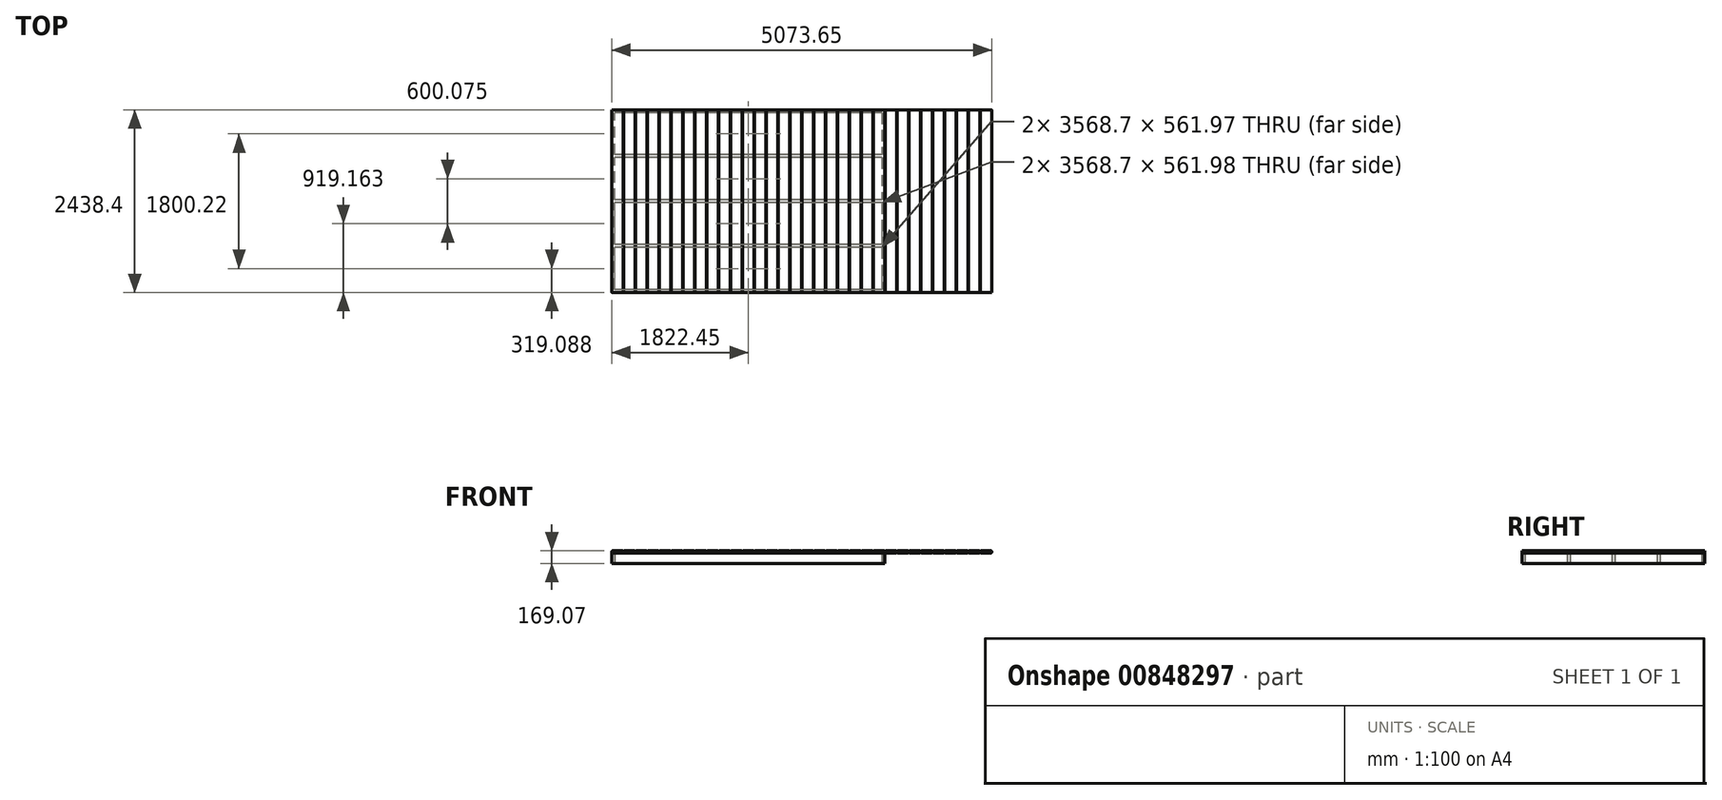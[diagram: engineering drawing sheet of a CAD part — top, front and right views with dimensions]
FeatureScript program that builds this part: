
annotation { "Feature Type Name" : "Feature", "Feature Type Description" : "" }
export const myFeature = defineFeature(function(context is Context, id is Id, definition is map)
    precondition{}
    {
        {
            var Q0;
            Q0=qCreatedBy(makeId("Top.planeOp"),FACE);
            var sketch = newSketch(context, id + "F0", { "sketchPlane" : qUnion([Q0])});
            skLineSegment(sketch, "E0.bottom", {"start": v(1784.35, 1181.1) * mm, "end": v(-1784.35, 1181.1) * mm});
            skLineSegment(sketch, "E0.top", {"start": v(1784.35, 1219.2) * mm, "end": v(-1784.35, 1219.2) * mm});
            skLineSegment(sketch, "E0.left", {"start": v(1784.35, 1181.1) * mm, "end": v(1784.35, 1219.2) * mm});
            skLineSegment(sketch, "E0.right", {"start": v(-1784.35, 1181.1) * mm, "end": v(-1784.35, 1219.2) * mm});
            skLineSegment(sketch, "E1.0.1.0", {"start": v(1784.35, 581.02) * mm, "end": v(-1784.35, 581.02) * mm});
            skLineSegment(sketch, "E1.0.1.1", {"start": v(1784.35, 619.12) * mm, "end": v(-1784.35, 619.12) * mm});
            skLineSegment(sketch, "E1.0.1.2", {"start": v(1784.35, 581.03) * mm, "end": v(1784.35, 619.12) * mm});
            skLineSegment(sketch, "E1.0.1.3", {"start": v(-1784.35, 581.02) * mm, "end": v(-1784.35, 619.12) * mm});
            skLineSegment(sketch, "E1.0.2.0", {"start": v(1784.35, -19.05) * mm, "end": v(-1784.35, -19.05) * mm});
            skLineSegment(sketch, "E1.0.2.1", {"start": v(1784.35, 19.05) * mm, "end": v(-1784.35, 19.05) * mm});
            skLineSegment(sketch, "E1.0.2.2", {"start": v(1784.35, -19.05) * mm, "end": v(1784.35, 19.05) * mm});
            skLineSegment(sketch, "E1.0.2.3", {"start": v(-1784.35, -19.05) * mm, "end": v(-1784.35, 19.05) * mm});
            skLineSegment(sketch, "E1.0.3.0", {"start": v(1784.35, -619.13) * mm, "end": v(-1784.35, -619.13) * mm});
            skLineSegment(sketch, "E1.0.3.1", {"start": v(1784.35, -581.03) * mm, "end": v(-1784.35, -581.03) * mm});
            skLineSegment(sketch, "E1.0.3.2", {"start": v(1784.35, -619.12) * mm, "end": v(1784.35, -581.03) * mm});
            skLineSegment(sketch, "E1.0.3.3", {"start": v(-1784.35, -619.13) * mm, "end": v(-1784.35, -581.03) * mm});
            skLineSegment(sketch, "E1.direction1", {"start": v(-1784.35, 1181.1) * mm, "end": v(110.9, 1181.1) * mm, "construction": true});
            skLineSegment(sketch, "E1.direction2", {"start": v(-1784.35, 1181.1) * mm, "end": v(-1784.35, 581.02) * mm, "construction": true});
            skLineSegment(sketch, "E2.0.0.4", {"start": v(1784.35, -1219.2) * mm, "end": v(-1784.35, -1219.2) * mm});
            skLineSegment(sketch, "E2.3.0.4", {"start": v(1784.35, -1181.1) * mm, "end": v(-1784.35, -1181.1) * mm});
            skLineSegment(sketch, "E2.6.0.4", {"start": v(1784.35, -1219.2) * mm, "end": v(1784.35, -1181.1) * mm});
            skLineSegment(sketch, "E2.9.0.4", {"start": v(-1784.35, -1219.2) * mm, "end": v(-1784.35, -1181.1) * mm});
            skLineSegment(sketch, "E3.bottom", {"start": v(-1784.35, -1219.2) * mm, "end": v(-1822.45, -1219.2) * mm});
            skLineSegment(sketch, "E3.top", {"start": v(-1784.35, 1219.2) * mm, "end": v(-1822.45, 1219.2) * mm});
            skLineSegment(sketch, "E3.left", {"start": v(-1784.35, -1219.2) * mm, "end": v(-1784.35, 1219.2) * mm});
            skLineSegment(sketch, "E3.right", {"start": v(-1822.45, -1219.2) * mm, "end": v(-1822.45, 1219.2) * mm});
            skLineSegment(sketch, "E4.bottom", {"start": v(1784.35, 1219.2) * mm, "end": v(1822.45, 1219.2) * mm});
            skLineSegment(sketch, "E4.top", {"start": v(1784.35, -1219.2) * mm, "end": v(1822.45, -1219.2) * mm});
            skLineSegment(sketch, "E4.left", {"start": v(1784.35, 1219.2) * mm, "end": v(1784.35, -1219.2) * mm});
            skLineSegment(sketch, "E4.right", {"start": v(1822.45, 1219.2) * mm, "end": v(1822.45, -1219.2) * mm});
            skLineSegment(sketch, "E5", {"start": v(1784.35, -1219.2) * mm, "end": v(-1784.35, 1219.2) * mm, "construction": true});
            skSolve(sketch);
        }
        {
            var Q0;
            {var subQ0=sQuery(id+"F0.wireOp",EDGE,"E0.bottom");Q0=makeQuery(id+"F0.imprint","IMPRINT",FACE,{"disambiguationData":[TD([[makeQuery(id+"F0.imprint","IMPRINT",EDGE,{"derivedFrom":subQ0}),-1.0]])]});}
            var Q1;
            {var subQ8=sQuery(id+"F0.wireOp",EDGE,"E3.bottom");Q1=makeQuery(id+"F0.imprint","IMPRINT",FACE,{"disambiguationData":[TD([[makeQuery(id+"F0.imprint","IMPRINT",EDGE,{"derivedFrom":subQ8}),-1.0]])]});}
            var Q2;
            {var subQ0=sQuery(id+"F0.wireOp",EDGE,"E1.0.1.0");Q2=makeQuery(id+"F0.imprint","IMPRINT",FACE,{"disambiguationData":[TD([[makeQuery(id+"F0.imprint","IMPRINT",EDGE,{"derivedFrom":subQ0}),-1.0]])]});}
            var Q3;
            {var subQ0=sQuery(id+"F0.wireOp",EDGE,"E1.0.2.0");Q3=makeQuery(id+"F0.imprint","IMPRINT",FACE,{"disambiguationData":[TD([[makeQuery(id+"F0.imprint","IMPRINT",EDGE,{"derivedFrom":subQ0}),-1.0]])]});}
            var Q4;
            {var subQ0=sQuery(id+"F0.wireOp",EDGE,"E1.0.3.0");Q4=makeQuery(id+"F0.imprint","IMPRINT",FACE,{"disambiguationData":[TD([[makeQuery(id+"F0.imprint","IMPRINT",EDGE,{"derivedFrom":subQ0}),-1.0]])]});}
            var Q5;
            {var subQ0=sQuery(id+"F0.wireOp",EDGE,"E2.0.0.4");Q5=makeQuery(id+"F0.imprint","IMPRINT",FACE,{"disambiguationData":[TD([[makeQuery(id+"F0.imprint","IMPRINT",EDGE,{"derivedFrom":subQ0}),-1.0]])]});}
            var Q6;
            {var subQ8=sQuery(id+"F0.wireOp",EDGE,"E4.bottom");Q6=makeQuery(id+"F0.imprint","IMPRINT",FACE,{"disambiguationData":[TD([[makeQuery(id+"F0.imprint","IMPRINT",EDGE,{"derivedFrom":subQ8}),-1.0]])]});}
            extrude(context, id + "F1", {"entities" : qUnion([Q0, Q1, Q2, Q3, Q4, Q5, Q6]), "depth" : 139.7 * mm, "offsetDistance" : 25.4 * mm});
        }
        {
            var Q0;
            Q0=makeQuery(id+"F1.opExtrude","SWEPT_FACE",FACE,{"disambiguationData":[OSD([sQuery(id+"F0.wireOp",EDGE,"E2.0.0.4"),sQuery(id+"F0.wireOp",EDGE,"E3.bottom"),sQuery(id+"F0.wireOp",EDGE,"E4.top")])]});
            var sketch = newSketch(context, id + "F2", { "sketchPlane" : qUnion([Q0])});
            skLineSegment(sketch, "E6.bottom", {"start": v(-1809.75, 139.7) * mm, "end": v(-1682.75, 139.7) * mm});
            skLineSegment(sketch, "E6.top", {"start": v(-1809.75, 169.07) * mm, "end": v(-1682.75, 169.07) * mm});
            skLineSegment(sketch, "E6.left", {"start": v(-1822.45, 152.4) * mm, "end": v(-1822.45, 156.37) * mm});
            skLineSegment(sketch, "E6.right", {"start": v(-1670.05, 152.4) * mm, "end": v(-1670.05, 156.37) * mm});
            skPoint(sketch, "E7.visualSharp", {"position": v(-1822.45, 169.07) * mm});
            skArc(sketch, "E7.filletArc", {"start": v(-1809.75, 169.07) * mm, "mid": v(-1818.73, 165.35) * mm, "end": v(-1822.45, 156.37) * mm});
            skPoint(sketch, "E8.visualSharp", {"position": v(-1670.05, 169.07) * mm});
            skArc(sketch, "E8.filletArc", {"start": v(-1670.05, 156.37) * mm, "mid": v(-1673.77, 165.35) * mm, "end": v(-1682.75, 169.07) * mm});
            skPoint(sketch, "E9.visualSharp", {"position": v(-1670.05, 139.7) * mm});
            skArc(sketch, "E9.filletArc", {"start": v(-1682.75, 139.7) * mm, "mid": v(-1673.77, 143.42) * mm, "end": v(-1670.05, 152.4) * mm});
            skPoint(sketch, "E10.visualSharp", {"position": v(-1822.45, 139.7) * mm});
            skArc(sketch, "E10.filletArc", {"start": v(-1822.45, 152.4) * mm, "mid": v(-1818.73, 143.42) * mm, "end": v(-1809.75, 139.7) * mm});
            skPoint(sketch, "E11.1.0.0", {"position": v(-1663.7, 139.7) * mm});
            skPoint(sketch, "E11.1.0.1", {"position": v(-1511.3, 139.7) * mm});
            skPoint(sketch, "E11.1.0.2", {"position": v(-1663.7, 169.07) * mm});
            skLineSegment(sketch, "E11.1.0.3", {"start": v(-1651, 169.07) * mm, "end": v(-1524, 169.07) * mm});
            skLineSegment(sketch, "E11.1.0.4", {"start": v(-1651, 139.7) * mm, "end": v(-1524, 139.7) * mm});
            skPoint(sketch, "E11.1.0.5", {"position": v(-1511.3, 169.07) * mm});
            skArc(sketch, "E11.1.0.6", {"start": v(-1663.7, 152.4) * mm, "mid": v(-1659.98, 143.42) * mm, "end": v(-1651, 139.7) * mm});
            skArc(sketch, "E11.1.0.7", {"start": v(-1524, 139.7) * mm, "mid": v(-1515.02, 143.42) * mm, "end": v(-1511.3, 152.4) * mm});
            skArc(sketch, "E11.1.0.8", {"start": v(-1651, 169.07) * mm, "mid": v(-1659.98, 165.35) * mm, "end": v(-1663.7, 156.37) * mm});
            skArc(sketch, "E11.1.0.9", {"start": v(-1511.3, 156.37) * mm, "mid": v(-1515.02, 165.35) * mm, "end": v(-1524, 169.07) * mm});
            skLineSegment(sketch, "E11.1.0.10", {"start": v(-1511.3, 152.4) * mm, "end": v(-1511.3, 156.37) * mm});
            skLineSegment(sketch, "E11.1.0.11", {"start": v(-1663.7, 152.4) * mm, "end": v(-1663.7, 156.37) * mm});
            skPoint(sketch, "E11.2.0.0", {"position": v(-1504.95, 139.7) * mm});
            skPoint(sketch, "E11.2.0.1", {"position": v(-1352.55, 139.7) * mm});
            skPoint(sketch, "E11.2.0.2", {"position": v(-1504.95, 169.07) * mm});
            skLineSegment(sketch, "E11.2.0.3", {"start": v(-1492.25, 169.07) * mm, "end": v(-1365.25, 169.07) * mm});
            skLineSegment(sketch, "E11.2.0.4", {"start": v(-1492.25, 139.7) * mm, "end": v(-1365.25, 139.7) * mm});
            skPoint(sketch, "E11.2.0.5", {"position": v(-1352.55, 169.07) * mm});
            skArc(sketch, "E11.2.0.6", {"start": v(-1504.95, 152.4) * mm, "mid": v(-1501.23, 143.42) * mm, "end": v(-1492.25, 139.7) * mm});
            skArc(sketch, "E11.2.0.7", {"start": v(-1365.25, 139.7) * mm, "mid": v(-1356.27, 143.42) * mm, "end": v(-1352.55, 152.4) * mm});
            skArc(sketch, "E11.2.0.8", {"start": v(-1492.25, 169.07) * mm, "mid": v(-1501.23, 165.35) * mm, "end": v(-1504.95, 156.37) * mm});
            skArc(sketch, "E11.2.0.9", {"start": v(-1352.55, 156.37) * mm, "mid": v(-1356.27, 165.35) * mm, "end": v(-1365.25, 169.07) * mm});
            skLineSegment(sketch, "E11.2.0.10", {"start": v(-1352.55, 152.4) * mm, "end": v(-1352.55, 156.37) * mm});
            skLineSegment(sketch, "E11.2.0.11", {"start": v(-1504.95, 152.4) * mm, "end": v(-1504.95, 156.37) * mm});
            skPoint(sketch, "E11.3.0.0", {"position": v(-1346.2, 139.7) * mm});
            skPoint(sketch, "E11.3.0.1", {"position": v(-1193.8, 139.7) * mm});
            skPoint(sketch, "E11.3.0.2", {"position": v(-1346.2, 169.07) * mm});
            skLineSegment(sketch, "E11.3.0.3", {"start": v(-1333.5, 169.07) * mm, "end": v(-1206.5, 169.07) * mm});
            skLineSegment(sketch, "E11.3.0.4", {"start": v(-1333.5, 139.7) * mm, "end": v(-1206.5, 139.7) * mm});
            skPoint(sketch, "E11.3.0.5", {"position": v(-1193.8, 169.07) * mm});
            skArc(sketch, "E11.3.0.6", {"start": v(-1346.2, 152.4) * mm, "mid": v(-1342.48, 143.42) * mm, "end": v(-1333.5, 139.7) * mm});
            skArc(sketch, "E11.3.0.7", {"start": v(-1206.5, 139.7) * mm, "mid": v(-1197.52, 143.42) * mm, "end": v(-1193.8, 152.4) * mm});
            skArc(sketch, "E11.3.0.8", {"start": v(-1333.5, 169.07) * mm, "mid": v(-1342.48, 165.35) * mm, "end": v(-1346.2, 156.37) * mm});
            skArc(sketch, "E11.3.0.9", {"start": v(-1193.8, 156.37) * mm, "mid": v(-1197.52, 165.35) * mm, "end": v(-1206.5, 169.07) * mm});
            skLineSegment(sketch, "E11.3.0.10", {"start": v(-1193.8, 152.4) * mm, "end": v(-1193.8, 156.37) * mm});
            skLineSegment(sketch, "E11.3.0.11", {"start": v(-1346.2, 152.4) * mm, "end": v(-1346.2, 156.37) * mm});
            skPoint(sketch, "E11.4.0.0", {"position": v(-1187.45, 139.7) * mm});
            skPoint(sketch, "E11.4.0.1", {"position": v(-1035.05, 139.7) * mm});
            skPoint(sketch, "E11.4.0.2", {"position": v(-1187.45, 169.07) * mm});
            skLineSegment(sketch, "E11.4.0.3", {"start": v(-1174.75, 169.07) * mm, "end": v(-1047.75, 169.07) * mm});
            skLineSegment(sketch, "E11.4.0.4", {"start": v(-1174.75, 139.7) * mm, "end": v(-1047.75, 139.7) * mm});
            skPoint(sketch, "E11.4.0.5", {"position": v(-1035.05, 169.07) * mm});
            skArc(sketch, "E11.4.0.6", {"start": v(-1187.45, 152.4) * mm, "mid": v(-1183.73, 143.42) * mm, "end": v(-1174.75, 139.7) * mm});
            skArc(sketch, "E11.4.0.7", {"start": v(-1047.75, 139.7) * mm, "mid": v(-1038.77, 143.42) * mm, "end": v(-1035.05, 152.4) * mm});
            skArc(sketch, "E11.4.0.8", {"start": v(-1174.75, 169.07) * mm, "mid": v(-1183.73, 165.35) * mm, "end": v(-1187.45, 156.37) * mm});
            skArc(sketch, "E11.4.0.9", {"start": v(-1035.05, 156.37) * mm, "mid": v(-1038.77, 165.35) * mm, "end": v(-1047.75, 169.07) * mm});
            skLineSegment(sketch, "E11.4.0.10", {"start": v(-1035.05, 152.4) * mm, "end": v(-1035.05, 156.37) * mm});
            skLineSegment(sketch, "E11.4.0.11", {"start": v(-1187.45, 152.4) * mm, "end": v(-1187.45, 156.37) * mm});
            skPoint(sketch, "E11.5.0.0", {"position": v(-1028.7, 139.7) * mm});
            skPoint(sketch, "E11.5.0.1", {"position": v(-876.3, 139.7) * mm});
            skPoint(sketch, "E11.5.0.2", {"position": v(-1028.7, 169.07) * mm});
            skLineSegment(sketch, "E11.5.0.3", {"start": v(-1016, 169.07) * mm, "end": v(-889, 169.07) * mm});
            skLineSegment(sketch, "E11.5.0.4", {"start": v(-1016, 139.7) * mm, "end": v(-889, 139.7) * mm});
            skPoint(sketch, "E11.5.0.5", {"position": v(-876.3, 169.07) * mm});
            skArc(sketch, "E11.5.0.6", {"start": v(-1028.7, 152.4) * mm, "mid": v(-1024.98, 143.42) * mm, "end": v(-1016, 139.7) * mm});
            skArc(sketch, "E11.5.0.7", {"start": v(-889, 139.7) * mm, "mid": v(-880.02, 143.42) * mm, "end": v(-876.3, 152.4) * mm});
            skArc(sketch, "E11.5.0.8", {"start": v(-1016, 169.07) * mm, "mid": v(-1024.98, 165.35) * mm, "end": v(-1028.7, 156.37) * mm});
            skArc(sketch, "E11.5.0.9", {"start": v(-876.3, 156.37) * mm, "mid": v(-880.02, 165.35) * mm, "end": v(-889, 169.07) * mm});
            skLineSegment(sketch, "E11.5.0.10", {"start": v(-876.3, 152.4) * mm, "end": v(-876.3, 156.37) * mm});
            skLineSegment(sketch, "E11.5.0.11", {"start": v(-1028.7, 152.4) * mm, "end": v(-1028.7, 156.37) * mm});
            skPoint(sketch, "E11.6.0.0", {"position": v(-869.95, 139.7) * mm});
            skPoint(sketch, "E11.6.0.1", {"position": v(-717.55, 139.7) * mm});
            skPoint(sketch, "E11.6.0.2", {"position": v(-869.95, 169.07) * mm});
            skLineSegment(sketch, "E11.6.0.3", {"start": v(-857.25, 169.07) * mm, "end": v(-730.25, 169.07) * mm});
            skLineSegment(sketch, "E11.6.0.4", {"start": v(-857.25, 139.7) * mm, "end": v(-730.25, 139.7) * mm});
            skPoint(sketch, "E11.6.0.5", {"position": v(-717.55, 169.07) * mm});
            skArc(sketch, "E11.6.0.6", {"start": v(-869.95, 152.4) * mm, "mid": v(-866.23, 143.42) * mm, "end": v(-857.25, 139.7) * mm});
            skArc(sketch, "E11.6.0.7", {"start": v(-730.25, 139.7) * mm, "mid": v(-721.27, 143.42) * mm, "end": v(-717.55, 152.4) * mm});
            skArc(sketch, "E11.6.0.8", {"start": v(-857.25, 169.07) * mm, "mid": v(-866.23, 165.35) * mm, "end": v(-869.95, 156.37) * mm});
            skArc(sketch, "E11.6.0.9", {"start": v(-717.55, 156.37) * mm, "mid": v(-721.27, 165.35) * mm, "end": v(-730.25, 169.07) * mm});
            skLineSegment(sketch, "E11.6.0.10", {"start": v(-717.55, 152.4) * mm, "end": v(-717.55, 156.37) * mm});
            skLineSegment(sketch, "E11.6.0.11", {"start": v(-869.95, 152.4) * mm, "end": v(-869.95, 156.37) * mm});
            skPoint(sketch, "E11.7.0.0", {"position": v(-711.2, 139.7) * mm});
            skPoint(sketch, "E11.7.0.1", {"position": v(-558.8, 139.7) * mm});
            skPoint(sketch, "E11.7.0.2", {"position": v(-711.2, 169.07) * mm});
            skLineSegment(sketch, "E11.7.0.3", {"start": v(-698.5, 169.07) * mm, "end": v(-571.5, 169.07) * mm});
            skLineSegment(sketch, "E11.7.0.4", {"start": v(-698.5, 139.7) * mm, "end": v(-571.5, 139.7) * mm});
            skPoint(sketch, "E11.7.0.5", {"position": v(-558.8, 169.07) * mm});
            skArc(sketch, "E11.7.0.6", {"start": v(-711.2, 152.4) * mm, "mid": v(-707.48, 143.42) * mm, "end": v(-698.5, 139.7) * mm});
            skArc(sketch, "E11.7.0.7", {"start": v(-571.5, 139.7) * mm, "mid": v(-562.52, 143.42) * mm, "end": v(-558.8, 152.4) * mm});
            skArc(sketch, "E11.7.0.8", {"start": v(-698.5, 169.07) * mm, "mid": v(-707.48, 165.35) * mm, "end": v(-711.2, 156.37) * mm});
            skArc(sketch, "E11.7.0.9", {"start": v(-558.8, 156.37) * mm, "mid": v(-562.52, 165.35) * mm, "end": v(-571.5, 169.07) * mm});
            skLineSegment(sketch, "E11.7.0.10", {"start": v(-558.8, 152.4) * mm, "end": v(-558.8, 156.37) * mm});
            skLineSegment(sketch, "E11.7.0.11", {"start": v(-711.2, 152.4) * mm, "end": v(-711.2, 156.37) * mm});
            skPoint(sketch, "E11.8.0.0", {"position": v(-552.45, 139.7) * mm});
            skPoint(sketch, "E11.8.0.1", {"position": v(-400.05, 139.7) * mm});
            skPoint(sketch, "E11.8.0.2", {"position": v(-552.45, 169.07) * mm});
            skLineSegment(sketch, "E11.8.0.3", {"start": v(-539.75, 169.07) * mm, "end": v(-412.75, 169.07) * mm});
            skLineSegment(sketch, "E11.8.0.4", {"start": v(-539.75, 139.7) * mm, "end": v(-412.75, 139.7) * mm});
            skPoint(sketch, "E11.8.0.5", {"position": v(-400.05, 169.07) * mm});
            skArc(sketch, "E11.8.0.6", {"start": v(-552.45, 152.4) * mm, "mid": v(-548.73, 143.42) * mm, "end": v(-539.75, 139.7) * mm});
            skArc(sketch, "E11.8.0.7", {"start": v(-412.75, 139.7) * mm, "mid": v(-403.77, 143.42) * mm, "end": v(-400.05, 152.4) * mm});
            skArc(sketch, "E11.8.0.8", {"start": v(-539.75, 169.07) * mm, "mid": v(-548.73, 165.35) * mm, "end": v(-552.45, 156.37) * mm});
            skArc(sketch, "E11.8.0.9", {"start": v(-400.05, 156.37) * mm, "mid": v(-403.77, 165.35) * mm, "end": v(-412.75, 169.07) * mm});
            skLineSegment(sketch, "E11.8.0.10", {"start": v(-400.05, 152.4) * mm, "end": v(-400.05, 156.37) * mm});
            skLineSegment(sketch, "E11.8.0.11", {"start": v(-552.45, 152.4) * mm, "end": v(-552.45, 156.37) * mm});
            skPoint(sketch, "E11.9.0.0", {"position": v(-393.7, 139.7) * mm});
            skPoint(sketch, "E11.9.0.1", {"position": v(-241.3, 139.7) * mm});
            skPoint(sketch, "E11.9.0.2", {"position": v(-393.7, 169.07) * mm});
            skLineSegment(sketch, "E11.9.0.3", {"start": v(-381, 169.07) * mm, "end": v(-254, 169.07) * mm});
            skLineSegment(sketch, "E11.9.0.4", {"start": v(-381, 139.7) * mm, "end": v(-254, 139.7) * mm});
            skPoint(sketch, "E11.9.0.5", {"position": v(-241.3, 169.07) * mm});
            skArc(sketch, "E11.9.0.6", {"start": v(-393.7, 152.4) * mm, "mid": v(-389.98, 143.42) * mm, "end": v(-381, 139.7) * mm});
            skArc(sketch, "E11.9.0.7", {"start": v(-254, 139.7) * mm, "mid": v(-245.02, 143.42) * mm, "end": v(-241.3, 152.4) * mm});
            skArc(sketch, "E11.9.0.8", {"start": v(-381, 169.07) * mm, "mid": v(-389.98, 165.35) * mm, "end": v(-393.7, 156.37) * mm});
            skArc(sketch, "E11.9.0.9", {"start": v(-241.3, 156.37) * mm, "mid": v(-245.02, 165.35) * mm, "end": v(-254, 169.07) * mm});
            skLineSegment(sketch, "E11.9.0.10", {"start": v(-241.3, 152.4) * mm, "end": v(-241.3, 156.37) * mm});
            skLineSegment(sketch, "E11.9.0.11", {"start": v(-393.7, 152.4) * mm, "end": v(-393.7, 156.37) * mm});
            skPoint(sketch, "E11.10.0.0", {"position": v(-234.95, 139.7) * mm});
            skPoint(sketch, "E11.10.0.1", {"position": v(-82.55, 139.7) * mm});
            skPoint(sketch, "E11.10.0.2", {"position": v(-234.95, 169.07) * mm});
            skLineSegment(sketch, "E11.10.0.3", {"start": v(-222.25, 169.07) * mm, "end": v(-95.25, 169.07) * mm});
            skLineSegment(sketch, "E11.10.0.4", {"start": v(-222.25, 139.7) * mm, "end": v(-95.25, 139.7) * mm});
            skPoint(sketch, "E11.10.0.5", {"position": v(-82.55, 169.07) * mm});
            skArc(sketch, "E11.10.0.6", {"start": v(-234.95, 152.4) * mm, "mid": v(-231.23, 143.42) * mm, "end": v(-222.25, 139.7) * mm});
            skArc(sketch, "E11.10.0.7", {"start": v(-95.25, 139.7) * mm, "mid": v(-86.27, 143.42) * mm, "end": v(-82.55, 152.4) * mm});
            skArc(sketch, "E11.10.0.8", {"start": v(-222.25, 169.07) * mm, "mid": v(-231.23, 165.35) * mm, "end": v(-234.95, 156.37) * mm});
            skArc(sketch, "E11.10.0.9", {"start": v(-82.55, 156.37) * mm, "mid": v(-86.27, 165.35) * mm, "end": v(-95.25, 169.07) * mm});
            skLineSegment(sketch, "E11.10.0.10", {"start": v(-82.55, 152.4) * mm, "end": v(-82.55, 156.37) * mm});
            skLineSegment(sketch, "E11.10.0.11", {"start": v(-234.95, 152.4) * mm, "end": v(-234.95, 156.37) * mm});
            skPoint(sketch, "E11.11.0.0", {"position": v(-76.2, 139.7) * mm});
            skPoint(sketch, "E11.11.0.1", {"position": v(76.2, 139.7) * mm});
            skPoint(sketch, "E11.11.0.2", {"position": v(-76.2, 169.07) * mm});
            skLineSegment(sketch, "E11.11.0.3", {"start": v(-63.5, 169.07) * mm, "end": v(63.5, 169.07) * mm});
            skLineSegment(sketch, "E11.11.0.4", {"start": v(-63.5, 139.7) * mm, "end": v(63.5, 139.7) * mm});
            skPoint(sketch, "E11.11.0.5", {"position": v(76.2, 169.07) * mm});
            skArc(sketch, "E11.11.0.6", {"start": v(-76.2, 152.4) * mm, "mid": v(-72.48, 143.42) * mm, "end": v(-63.5, 139.7) * mm});
            skArc(sketch, "E11.11.0.7", {"start": v(63.5, 139.7) * mm, "mid": v(72.48, 143.42) * mm, "end": v(76.2, 152.4) * mm});
            skArc(sketch, "E11.11.0.8", {"start": v(-63.5, 169.07) * mm, "mid": v(-72.48, 165.35) * mm, "end": v(-76.2, 156.37) * mm});
            skArc(sketch, "E11.11.0.9", {"start": v(76.2, 156.37) * mm, "mid": v(72.48, 165.35) * mm, "end": v(63.5, 169.07) * mm});
            skLineSegment(sketch, "E11.11.0.10", {"start": v(76.2, 152.4) * mm, "end": v(76.2, 156.37) * mm});
            skLineSegment(sketch, "E11.11.0.11", {"start": v(-76.2, 152.4) * mm, "end": v(-76.2, 156.37) * mm});
            skPoint(sketch, "E11.12.0.0", {"position": v(82.55, 139.7) * mm});
            skPoint(sketch, "E11.12.0.1", {"position": v(234.95, 139.7) * mm});
            skPoint(sketch, "E11.12.0.2", {"position": v(82.55, 169.07) * mm});
            skLineSegment(sketch, "E11.12.0.3", {"start": v(95.25, 169.07) * mm, "end": v(222.25, 169.07) * mm});
            skLineSegment(sketch, "E11.12.0.4", {"start": v(95.25, 139.7) * mm, "end": v(222.25, 139.7) * mm});
            skPoint(sketch, "E11.12.0.5", {"position": v(234.95, 169.07) * mm});
            skArc(sketch, "E11.12.0.6", {"start": v(82.55, 152.4) * mm, "mid": v(86.27, 143.42) * mm, "end": v(95.25, 139.7) * mm});
            skArc(sketch, "E11.12.0.7", {"start": v(222.25, 139.7) * mm, "mid": v(231.23, 143.42) * mm, "end": v(234.95, 152.4) * mm});
            skArc(sketch, "E11.12.0.8", {"start": v(95.25, 169.07) * mm, "mid": v(86.27, 165.35) * mm, "end": v(82.55, 156.37) * mm});
            skArc(sketch, "E11.12.0.9", {"start": v(234.95, 156.37) * mm, "mid": v(231.23, 165.35) * mm, "end": v(222.25, 169.07) * mm});
            skLineSegment(sketch, "E11.12.0.10", {"start": v(234.95, 152.4) * mm, "end": v(234.95, 156.37) * mm});
            skLineSegment(sketch, "E11.12.0.11", {"start": v(82.55, 152.4) * mm, "end": v(82.55, 156.37) * mm});
            skPoint(sketch, "E11.13.0.0", {"position": v(241.3, 139.7) * mm});
            skPoint(sketch, "E11.13.0.1", {"position": v(393.7, 139.7) * mm});
            skPoint(sketch, "E11.13.0.2", {"position": v(241.3, 169.07) * mm});
            skLineSegment(sketch, "E11.13.0.3", {"start": v(254, 169.07) * mm, "end": v(381, 169.07) * mm});
            skLineSegment(sketch, "E11.13.0.4", {"start": v(254, 139.7) * mm, "end": v(381, 139.7) * mm});
            skPoint(sketch, "E11.13.0.5", {"position": v(393.7, 169.07) * mm});
            skArc(sketch, "E11.13.0.6", {"start": v(241.3, 152.4) * mm, "mid": v(245.02, 143.42) * mm, "end": v(254, 139.7) * mm});
            skArc(sketch, "E11.13.0.7", {"start": v(381, 139.7) * mm, "mid": v(389.98, 143.42) * mm, "end": v(393.7, 152.4) * mm});
            skArc(sketch, "E11.13.0.8", {"start": v(254, 169.07) * mm, "mid": v(245.02, 165.35) * mm, "end": v(241.3, 156.37) * mm});
            skArc(sketch, "E11.13.0.9", {"start": v(393.7, 156.37) * mm, "mid": v(389.98, 165.35) * mm, "end": v(381, 169.07) * mm});
            skLineSegment(sketch, "E11.13.0.10", {"start": v(393.7, 152.4) * mm, "end": v(393.7, 156.37) * mm});
            skLineSegment(sketch, "E11.13.0.11", {"start": v(241.3, 152.4) * mm, "end": v(241.3, 156.37) * mm});
            skPoint(sketch, "E11.14.0.0", {"position": v(400.05, 139.7) * mm});
            skPoint(sketch, "E11.14.0.1", {"position": v(552.45, 139.7) * mm});
            skPoint(sketch, "E11.14.0.2", {"position": v(400.05, 169.07) * mm});
            skLineSegment(sketch, "E11.14.0.3", {"start": v(412.75, 169.07) * mm, "end": v(539.75, 169.07) * mm});
            skLineSegment(sketch, "E11.14.0.4", {"start": v(412.75, 139.7) * mm, "end": v(539.75, 139.7) * mm});
            skPoint(sketch, "E11.14.0.5", {"position": v(552.45, 169.07) * mm});
            skArc(sketch, "E11.14.0.6", {"start": v(400.05, 152.4) * mm, "mid": v(403.77, 143.42) * mm, "end": v(412.75, 139.7) * mm});
            skArc(sketch, "E11.14.0.7", {"start": v(539.75, 139.7) * mm, "mid": v(548.73, 143.42) * mm, "end": v(552.45, 152.4) * mm});
            skArc(sketch, "E11.14.0.8", {"start": v(412.75, 169.07) * mm, "mid": v(403.77, 165.35) * mm, "end": v(400.05, 156.37) * mm});
            skArc(sketch, "E11.14.0.9", {"start": v(552.45, 156.37) * mm, "mid": v(548.73, 165.35) * mm, "end": v(539.75, 169.07) * mm});
            skLineSegment(sketch, "E11.14.0.10", {"start": v(552.45, 152.4) * mm, "end": v(552.45, 156.37) * mm});
            skLineSegment(sketch, "E11.14.0.11", {"start": v(400.05, 152.4) * mm, "end": v(400.05, 156.37) * mm});
            skPoint(sketch, "E11.15.0.0", {"position": v(558.8, 139.7) * mm});
            skPoint(sketch, "E11.15.0.1", {"position": v(711.2, 139.7) * mm});
            skPoint(sketch, "E11.15.0.2", {"position": v(558.8, 169.07) * mm});
            skLineSegment(sketch, "E11.15.0.3", {"start": v(571.5, 169.07) * mm, "end": v(698.5, 169.07) * mm});
            skLineSegment(sketch, "E11.15.0.4", {"start": v(571.5, 139.7) * mm, "end": v(698.5, 139.7) * mm});
            skPoint(sketch, "E11.15.0.5", {"position": v(711.2, 169.07) * mm});
            skArc(sketch, "E11.15.0.6", {"start": v(558.8, 152.4) * mm, "mid": v(562.52, 143.42) * mm, "end": v(571.5, 139.7) * mm});
            skArc(sketch, "E11.15.0.7", {"start": v(698.5, 139.7) * mm, "mid": v(707.48, 143.42) * mm, "end": v(711.2, 152.4) * mm});
            skArc(sketch, "E11.15.0.8", {"start": v(571.5, 169.07) * mm, "mid": v(562.52, 165.35) * mm, "end": v(558.8, 156.37) * mm});
            skArc(sketch, "E11.15.0.9", {"start": v(711.2, 156.37) * mm, "mid": v(707.48, 165.35) * mm, "end": v(698.5, 169.07) * mm});
            skLineSegment(sketch, "E11.15.0.10", {"start": v(711.2, 152.4) * mm, "end": v(711.2, 156.37) * mm});
            skLineSegment(sketch, "E11.15.0.11", {"start": v(558.8, 152.4) * mm, "end": v(558.8, 156.37) * mm});
            skPoint(sketch, "E11.16.0.0", {"position": v(717.55, 139.7) * mm});
            skPoint(sketch, "E11.16.0.1", {"position": v(869.95, 139.7) * mm});
            skPoint(sketch, "E11.16.0.2", {"position": v(717.55, 169.07) * mm});
            skLineSegment(sketch, "E11.16.0.3", {"start": v(730.25, 169.07) * mm, "end": v(857.25, 169.07) * mm});
            skLineSegment(sketch, "E11.16.0.4", {"start": v(730.25, 139.7) * mm, "end": v(857.25, 139.7) * mm});
            skPoint(sketch, "E11.16.0.5", {"position": v(869.95, 169.07) * mm});
            skArc(sketch, "E11.16.0.6", {"start": v(717.55, 152.4) * mm, "mid": v(721.27, 143.42) * mm, "end": v(730.25, 139.7) * mm});
            skArc(sketch, "E11.16.0.7", {"start": v(857.25, 139.7) * mm, "mid": v(866.23, 143.42) * mm, "end": v(869.95, 152.4) * mm});
            skArc(sketch, "E11.16.0.8", {"start": v(730.25, 169.07) * mm, "mid": v(721.27, 165.35) * mm, "end": v(717.55, 156.37) * mm});
            skArc(sketch, "E11.16.0.9", {"start": v(869.95, 156.37) * mm, "mid": v(866.23, 165.35) * mm, "end": v(857.25, 169.07) * mm});
            skLineSegment(sketch, "E11.16.0.10", {"start": v(869.95, 152.4) * mm, "end": v(869.95, 156.37) * mm});
            skLineSegment(sketch, "E11.16.0.11", {"start": v(717.55, 152.4) * mm, "end": v(717.55, 156.37) * mm});
            skPoint(sketch, "E11.17.0.0", {"position": v(876.3, 139.7) * mm});
            skPoint(sketch, "E11.17.0.1", {"position": v(1028.7, 139.7) * mm});
            skPoint(sketch, "E11.17.0.2", {"position": v(876.3, 169.07) * mm});
            skLineSegment(sketch, "E11.17.0.3", {"start": v(889, 169.07) * mm, "end": v(1016, 169.07) * mm});
            skLineSegment(sketch, "E11.17.0.4", {"start": v(889, 139.7) * mm, "end": v(1016, 139.7) * mm});
            skPoint(sketch, "E11.17.0.5", {"position": v(1028.7, 169.07) * mm});
            skArc(sketch, "E11.17.0.6", {"start": v(876.3, 152.4) * mm, "mid": v(880.02, 143.42) * mm, "end": v(889, 139.7) * mm});
            skArc(sketch, "E11.17.0.7", {"start": v(1016, 139.7) * mm, "mid": v(1024.98, 143.42) * mm, "end": v(1028.7, 152.4) * mm});
            skArc(sketch, "E11.17.0.8", {"start": v(889, 169.07) * mm, "mid": v(880.02, 165.35) * mm, "end": v(876.3, 156.37) * mm});
            skArc(sketch, "E11.17.0.9", {"start": v(1028.7, 156.37) * mm, "mid": v(1024.98, 165.35) * mm, "end": v(1016, 169.07) * mm});
            skLineSegment(sketch, "E11.17.0.10", {"start": v(1028.7, 152.4) * mm, "end": v(1028.7, 156.37) * mm});
            skLineSegment(sketch, "E11.17.0.11", {"start": v(876.3, 152.4) * mm, "end": v(876.3, 156.37) * mm});
            skPoint(sketch, "E11.18.0.0", {"position": v(1035.05, 139.7) * mm});
            skPoint(sketch, "E11.18.0.1", {"position": v(1187.45, 139.7) * mm});
            skPoint(sketch, "E11.18.0.2", {"position": v(1035.05, 169.07) * mm});
            skLineSegment(sketch, "E11.18.0.3", {"start": v(1047.75, 169.07) * mm, "end": v(1174.75, 169.07) * mm});
            skLineSegment(sketch, "E11.18.0.4", {"start": v(1047.75, 139.7) * mm, "end": v(1174.75, 139.7) * mm});
            skPoint(sketch, "E11.18.0.5", {"position": v(1187.45, 169.07) * mm});
            skArc(sketch, "E11.18.0.6", {"start": v(1035.05, 152.4) * mm, "mid": v(1038.77, 143.42) * mm, "end": v(1047.75, 139.7) * mm});
            skArc(sketch, "E11.18.0.7", {"start": v(1174.75, 139.7) * mm, "mid": v(1183.73, 143.42) * mm, "end": v(1187.45, 152.4) * mm});
            skArc(sketch, "E11.18.0.8", {"start": v(1047.75, 169.07) * mm, "mid": v(1038.77, 165.35) * mm, "end": v(1035.05, 156.37) * mm});
            skArc(sketch, "E11.18.0.9", {"start": v(1187.45, 156.37) * mm, "mid": v(1183.73, 165.35) * mm, "end": v(1174.75, 169.07) * mm});
            skLineSegment(sketch, "E11.18.0.10", {"start": v(1187.45, 152.4) * mm, "end": v(1187.45, 156.37) * mm});
            skLineSegment(sketch, "E11.18.0.11", {"start": v(1035.05, 152.4) * mm, "end": v(1035.05, 156.37) * mm});
            skPoint(sketch, "E11.19.0.0", {"position": v(1193.8, 139.7) * mm});
            skPoint(sketch, "E11.19.0.1", {"position": v(1346.2, 139.7) * mm});
            skPoint(sketch, "E11.19.0.2", {"position": v(1193.8, 169.07) * mm});
            skLineSegment(sketch, "E11.19.0.3", {"start": v(1206.5, 169.07) * mm, "end": v(1333.5, 169.07) * mm});
            skLineSegment(sketch, "E11.19.0.4", {"start": v(1206.5, 139.7) * mm, "end": v(1333.5, 139.7) * mm});
            skPoint(sketch, "E11.19.0.5", {"position": v(1346.2, 169.07) * mm});
            skArc(sketch, "E11.19.0.6", {"start": v(1193.8, 152.4) * mm, "mid": v(1197.52, 143.42) * mm, "end": v(1206.5, 139.7) * mm});
            skArc(sketch, "E11.19.0.7", {"start": v(1333.5, 139.7) * mm, "mid": v(1342.48, 143.42) * mm, "end": v(1346.2, 152.4) * mm});
            skArc(sketch, "E11.19.0.8", {"start": v(1206.5, 169.07) * mm, "mid": v(1197.52, 165.35) * mm, "end": v(1193.8, 156.37) * mm});
            skArc(sketch, "E11.19.0.9", {"start": v(1346.2, 156.37) * mm, "mid": v(1342.48, 165.35) * mm, "end": v(1333.5, 169.07) * mm});
            skLineSegment(sketch, "E11.19.0.10", {"start": v(1346.2, 152.4) * mm, "end": v(1346.2, 156.37) * mm});
            skLineSegment(sketch, "E11.19.0.11", {"start": v(1193.8, 152.4) * mm, "end": v(1193.8, 156.37) * mm});
            skPoint(sketch, "E11.20.0.0", {"position": v(1352.55, 139.7) * mm});
            skPoint(sketch, "E11.20.0.1", {"position": v(1504.95, 139.7) * mm});
            skPoint(sketch, "E11.20.0.2", {"position": v(1352.55, 169.07) * mm});
            skLineSegment(sketch, "E11.20.0.3", {"start": v(1365.25, 169.07) * mm, "end": v(1492.25, 169.07) * mm});
            skLineSegment(sketch, "E11.20.0.4", {"start": v(1365.25, 139.7) * mm, "end": v(1492.25, 139.7) * mm});
            skPoint(sketch, "E11.20.0.5", {"position": v(1504.95, 169.07) * mm});
            skArc(sketch, "E11.20.0.6", {"start": v(1352.55, 152.4) * mm, "mid": v(1356.27, 143.42) * mm, "end": v(1365.25, 139.7) * mm});
            skArc(sketch, "E11.20.0.7", {"start": v(1492.25, 139.7) * mm, "mid": v(1501.23, 143.42) * mm, "end": v(1504.95, 152.4) * mm});
            skArc(sketch, "E11.20.0.8", {"start": v(1365.25, 169.07) * mm, "mid": v(1356.27, 165.35) * mm, "end": v(1352.55, 156.37) * mm});
            skArc(sketch, "E11.20.0.9", {"start": v(1504.95, 156.37) * mm, "mid": v(1501.23, 165.35) * mm, "end": v(1492.25, 169.07) * mm});
            skLineSegment(sketch, "E11.20.0.10", {"start": v(1504.95, 152.4) * mm, "end": v(1504.95, 156.37) * mm});
            skLineSegment(sketch, "E11.20.0.11", {"start": v(1352.55, 152.4) * mm, "end": v(1352.55, 156.37) * mm});
            skPoint(sketch, "E11.21.0.0", {"position": v(1511.3, 139.7) * mm});
            skPoint(sketch, "E11.21.0.1", {"position": v(1663.7, 139.7) * mm});
            skPoint(sketch, "E11.21.0.2", {"position": v(1511.3, 169.07) * mm});
            skLineSegment(sketch, "E11.21.0.3", {"start": v(1524, 169.07) * mm, "end": v(1651, 169.07) * mm});
            skLineSegment(sketch, "E11.21.0.4", {"start": v(1524, 139.7) * mm, "end": v(1651, 139.7) * mm});
            skPoint(sketch, "E11.21.0.5", {"position": v(1663.7, 169.07) * mm});
            skArc(sketch, "E11.21.0.6", {"start": v(1511.3, 152.4) * mm, "mid": v(1515.02, 143.42) * mm, "end": v(1524, 139.7) * mm});
            skArc(sketch, "E11.21.0.7", {"start": v(1651, 139.7) * mm, "mid": v(1659.98, 143.42) * mm, "end": v(1663.7, 152.4) * mm});
            skArc(sketch, "E11.21.0.8", {"start": v(1524, 169.07) * mm, "mid": v(1515.02, 165.35) * mm, "end": v(1511.3, 156.37) * mm});
            skArc(sketch, "E11.21.0.9", {"start": v(1663.7, 156.37) * mm, "mid": v(1659.98, 165.35) * mm, "end": v(1651, 169.07) * mm});
            skLineSegment(sketch, "E11.21.0.10", {"start": v(1663.7, 152.4) * mm, "end": v(1663.7, 156.37) * mm});
            skLineSegment(sketch, "E11.21.0.11", {"start": v(1511.3, 152.4) * mm, "end": v(1511.3, 156.37) * mm});
            skPoint(sketch, "E11.22.0.0", {"position": v(1670.05, 139.7) * mm});
            skPoint(sketch, "E11.22.0.1", {"position": v(1822.45, 139.7) * mm});
            skPoint(sketch, "E11.22.0.2", {"position": v(1670.05, 169.07) * mm});
            skLineSegment(sketch, "E11.22.0.3", {"start": v(1682.75, 169.07) * mm, "end": v(1809.75, 169.07) * mm});
            skLineSegment(sketch, "E11.22.0.4", {"start": v(1682.75, 139.7) * mm, "end": v(1809.75, 139.7) * mm});
            skPoint(sketch, "E11.22.0.5", {"position": v(1822.45, 169.07) * mm});
            skArc(sketch, "E11.22.0.6", {"start": v(1670.05, 152.4) * mm, "mid": v(1673.77, 143.42) * mm, "end": v(1682.75, 139.7) * mm});
            skArc(sketch, "E11.22.0.7", {"start": v(1809.75, 139.7) * mm, "mid": v(1818.73, 143.42) * mm, "end": v(1822.45, 152.4) * mm});
            skArc(sketch, "E11.22.0.8", {"start": v(1682.75, 169.07) * mm, "mid": v(1673.77, 165.35) * mm, "end": v(1670.05, 156.37) * mm});
            skArc(sketch, "E11.22.0.9", {"start": v(1822.45, 156.37) * mm, "mid": v(1818.73, 165.35) * mm, "end": v(1809.75, 169.07) * mm});
            skLineSegment(sketch, "E11.22.0.10", {"start": v(1822.45, 152.4) * mm, "end": v(1822.45, 156.37) * mm});
            skLineSegment(sketch, "E11.22.0.11", {"start": v(1670.05, 152.4) * mm, "end": v(1670.05, 156.37) * mm});
            skLineSegment(sketch, "E11.direction1", {"start": v(-1822.45, 139.7) * mm, "end": v(-1663.7, 139.7) * mm, "construction": true});
            skPoint(sketch, "E12.0.23.0", {"position": v(1828.8, 139.7) * mm});
            skPoint(sketch, "E12.1.23.0", {"position": v(1981.2, 139.7) * mm});
            skPoint(sketch, "E12.2.23.0", {"position": v(1828.8, 169.07) * mm});
            skLineSegment(sketch, "E12.3.23.0", {"start": v(1841.5, 169.07) * mm, "end": v(1968.5, 169.07) * mm});
            skLineSegment(sketch, "E12.6.23.0", {"start": v(1841.5, 139.7) * mm, "end": v(1968.5, 139.7) * mm});
            skPoint(sketch, "E12.9.23.0", {"position": v(1981.2, 169.07) * mm});
            skArc(sketch, "E12.10.23.0", {"start": v(1828.8, 152.4) * mm, "mid": v(1832.52, 143.42) * mm, "end": v(1841.5, 139.7) * mm});
            skArc(sketch, "E12.14.23.0", {"start": v(1968.5, 139.7) * mm, "mid": v(1977.48, 143.42) * mm, "end": v(1981.2, 152.4) * mm});
            skArc(sketch, "E12.18.23.0", {"start": v(1841.5, 169.07) * mm, "mid": v(1832.52, 165.35) * mm, "end": v(1828.8, 156.37) * mm});
            skArc(sketch, "E12.22.23.0", {"start": v(1981.2, 156.37) * mm, "mid": v(1977.48, 165.35) * mm, "end": v(1968.5, 169.07) * mm});
            skLineSegment(sketch, "E12.26.23.0", {"start": v(1981.2, 152.4) * mm, "end": v(1981.2, 156.37) * mm});
            skLineSegment(sketch, "E12.29.23.0", {"start": v(1828.8, 152.4) * mm, "end": v(1828.8, 156.37) * mm});
            skPoint(sketch, "E12.0.24.0", {"position": v(1987.55, 139.7) * mm});
            skPoint(sketch, "E12.1.24.0", {"position": v(2139.95, 139.7) * mm});
            skPoint(sketch, "E12.2.24.0", {"position": v(1987.55, 169.07) * mm});
            skLineSegment(sketch, "E12.3.24.0", {"start": v(2000.25, 169.07) * mm, "end": v(2127.25, 169.07) * mm});
            skLineSegment(sketch, "E12.6.24.0", {"start": v(2000.25, 139.7) * mm, "end": v(2127.25, 139.7) * mm});
            skPoint(sketch, "E12.9.24.0", {"position": v(2139.95, 169.07) * mm});
            skArc(sketch, "E12.10.24.0", {"start": v(1987.55, 152.4) * mm, "mid": v(1991.27, 143.42) * mm, "end": v(2000.25, 139.7) * mm});
            skArc(sketch, "E12.14.24.0", {"start": v(2127.25, 139.7) * mm, "mid": v(2136.23, 143.42) * mm, "end": v(2139.95, 152.4) * mm});
            skArc(sketch, "E12.18.24.0", {"start": v(2000.25, 169.07) * mm, "mid": v(1991.27, 165.35) * mm, "end": v(1987.55, 156.37) * mm});
            skArc(sketch, "E12.22.24.0", {"start": v(2139.95, 156.37) * mm, "mid": v(2136.23, 165.35) * mm, "end": v(2127.25, 169.07) * mm});
            skLineSegment(sketch, "E12.26.24.0", {"start": v(2139.95, 152.4) * mm, "end": v(2139.95, 156.37) * mm});
            skLineSegment(sketch, "E12.29.24.0", {"start": v(1987.55, 152.4) * mm, "end": v(1987.55, 156.37) * mm});
            skPoint(sketch, "E12.0.25.0", {"position": v(2146.3, 139.7) * mm});
            skPoint(sketch, "E12.1.25.0", {"position": v(2298.7, 139.7) * mm});
            skPoint(sketch, "E12.2.25.0", {"position": v(2146.3, 169.07) * mm});
            skLineSegment(sketch, "E12.3.25.0", {"start": v(2159, 169.07) * mm, "end": v(2286, 169.07) * mm});
            skLineSegment(sketch, "E12.6.25.0", {"start": v(2159, 139.7) * mm, "end": v(2286, 139.7) * mm});
            skPoint(sketch, "E12.9.25.0", {"position": v(2298.7, 169.07) * mm});
            skArc(sketch, "E12.10.25.0", {"start": v(2146.3, 152.4) * mm, "mid": v(2150.02, 143.42) * mm, "end": v(2159, 139.7) * mm});
            skArc(sketch, "E12.14.25.0", {"start": v(2286, 139.7) * mm, "mid": v(2294.98, 143.42) * mm, "end": v(2298.7, 152.4) * mm});
            skArc(sketch, "E12.18.25.0", {"start": v(2159, 169.07) * mm, "mid": v(2150.02, 165.35) * mm, "end": v(2146.3, 156.37) * mm});
            skArc(sketch, "E12.22.25.0", {"start": v(2298.7, 156.37) * mm, "mid": v(2294.98, 165.35) * mm, "end": v(2286, 169.07) * mm});
            skLineSegment(sketch, "E12.26.25.0", {"start": v(2298.7, 152.4) * mm, "end": v(2298.7, 156.37) * mm});
            skLineSegment(sketch, "E12.29.25.0", {"start": v(2146.3, 152.4) * mm, "end": v(2146.3, 156.37) * mm});
            skPoint(sketch, "E12.0.26.0", {"position": v(2305.05, 139.7) * mm});
            skPoint(sketch, "E12.1.26.0", {"position": v(2457.45, 139.7) * mm});
            skPoint(sketch, "E12.2.26.0", {"position": v(2305.05, 169.07) * mm});
            skLineSegment(sketch, "E12.3.26.0", {"start": v(2317.75, 169.07) * mm, "end": v(2444.75, 169.07) * mm});
            skLineSegment(sketch, "E12.6.26.0", {"start": v(2317.75, 139.7) * mm, "end": v(2444.75, 139.7) * mm});
            skPoint(sketch, "E12.9.26.0", {"position": v(2457.45, 169.07) * mm});
            skArc(sketch, "E12.10.26.0", {"start": v(2305.05, 152.4) * mm, "mid": v(2308.77, 143.42) * mm, "end": v(2317.75, 139.7) * mm});
            skArc(sketch, "E12.14.26.0", {"start": v(2444.75, 139.7) * mm, "mid": v(2453.73, 143.42) * mm, "end": v(2457.45, 152.4) * mm});
            skArc(sketch, "E12.18.26.0", {"start": v(2317.75, 169.07) * mm, "mid": v(2308.77, 165.35) * mm, "end": v(2305.05, 156.37) * mm});
            skArc(sketch, "E12.22.26.0", {"start": v(2457.45, 156.37) * mm, "mid": v(2453.73, 165.35) * mm, "end": v(2444.75, 169.07) * mm});
            skLineSegment(sketch, "E12.26.26.0", {"start": v(2457.45, 152.4) * mm, "end": v(2457.45, 156.37) * mm});
            skLineSegment(sketch, "E12.29.26.0", {"start": v(2305.05, 152.4) * mm, "end": v(2305.05, 156.37) * mm});
            skPoint(sketch, "E12.0.27.0", {"position": v(2463.8, 139.7) * mm});
            skPoint(sketch, "E12.1.27.0", {"position": v(2616.2, 139.7) * mm});
            skPoint(sketch, "E12.2.27.0", {"position": v(2463.8, 169.07) * mm});
            skLineSegment(sketch, "E12.3.27.0", {"start": v(2476.5, 169.07) * mm, "end": v(2603.5, 169.07) * mm});
            skLineSegment(sketch, "E12.6.27.0", {"start": v(2476.5, 139.7) * mm, "end": v(2603.5, 139.7) * mm});
            skPoint(sketch, "E12.9.27.0", {"position": v(2616.2, 169.07) * mm});
            skArc(sketch, "E12.10.27.0", {"start": v(2463.8, 152.4) * mm, "mid": v(2467.52, 143.42) * mm, "end": v(2476.5, 139.7) * mm});
            skArc(sketch, "E12.14.27.0", {"start": v(2603.5, 139.7) * mm, "mid": v(2612.48, 143.42) * mm, "end": v(2616.2, 152.4) * mm});
            skArc(sketch, "E12.18.27.0", {"start": v(2476.5, 169.07) * mm, "mid": v(2467.52, 165.35) * mm, "end": v(2463.8, 156.37) * mm});
            skArc(sketch, "E12.22.27.0", {"start": v(2616.2, 156.37) * mm, "mid": v(2612.48, 165.35) * mm, "end": v(2603.5, 169.07) * mm});
            skLineSegment(sketch, "E12.26.27.0", {"start": v(2616.2, 152.4) * mm, "end": v(2616.2, 156.37) * mm});
            skLineSegment(sketch, "E12.29.27.0", {"start": v(2463.8, 152.4) * mm, "end": v(2463.8, 156.37) * mm});
            skPoint(sketch, "E12.0.28.0", {"position": v(2622.55, 139.7) * mm});
            skPoint(sketch, "E12.1.28.0", {"position": v(2774.95, 139.7) * mm});
            skPoint(sketch, "E12.2.28.0", {"position": v(2622.55, 169.07) * mm});
            skLineSegment(sketch, "E12.3.28.0", {"start": v(2635.25, 169.07) * mm, "end": v(2762.25, 169.07) * mm});
            skLineSegment(sketch, "E12.6.28.0", {"start": v(2635.25, 139.7) * mm, "end": v(2762.25, 139.7) * mm});
            skPoint(sketch, "E12.9.28.0", {"position": v(2774.95, 169.07) * mm});
            skArc(sketch, "E12.10.28.0", {"start": v(2622.55, 152.4) * mm, "mid": v(2626.27, 143.42) * mm, "end": v(2635.25, 139.7) * mm});
            skArc(sketch, "E12.14.28.0", {"start": v(2762.25, 139.7) * mm, "mid": v(2771.23, 143.42) * mm, "end": v(2774.95, 152.4) * mm});
            skArc(sketch, "E12.18.28.0", {"start": v(2635.25, 169.07) * mm, "mid": v(2626.27, 165.35) * mm, "end": v(2622.55, 156.37) * mm});
            skArc(sketch, "E12.22.28.0", {"start": v(2774.95, 156.37) * mm, "mid": v(2771.23, 165.35) * mm, "end": v(2762.25, 169.07) * mm});
            skLineSegment(sketch, "E12.26.28.0", {"start": v(2774.95, 152.4) * mm, "end": v(2774.95, 156.37) * mm});
            skLineSegment(sketch, "E12.29.28.0", {"start": v(2622.55, 152.4) * mm, "end": v(2622.55, 156.37) * mm});
            skPoint(sketch, "E12.0.29.0", {"position": v(2781.3, 139.7) * mm});
            skPoint(sketch, "E12.1.29.0", {"position": v(2933.7, 139.7) * mm});
            skPoint(sketch, "E12.2.29.0", {"position": v(2781.3, 169.07) * mm});
            skLineSegment(sketch, "E12.3.29.0", {"start": v(2794, 169.07) * mm, "end": v(2921, 169.07) * mm});
            skLineSegment(sketch, "E12.6.29.0", {"start": v(2794, 139.7) * mm, "end": v(2921, 139.7) * mm});
            skPoint(sketch, "E12.9.29.0", {"position": v(2933.7, 169.07) * mm});
            skArc(sketch, "E12.10.29.0", {"start": v(2781.3, 152.4) * mm, "mid": v(2785.02, 143.42) * mm, "end": v(2794, 139.7) * mm});
            skArc(sketch, "E12.14.29.0", {"start": v(2921, 139.7) * mm, "mid": v(2929.98, 143.42) * mm, "end": v(2933.7, 152.4) * mm});
            skArc(sketch, "E12.18.29.0", {"start": v(2794, 169.07) * mm, "mid": v(2785.02, 165.35) * mm, "end": v(2781.3, 156.37) * mm});
            skArc(sketch, "E12.22.29.0", {"start": v(2933.7, 156.37) * mm, "mid": v(2929.98, 165.35) * mm, "end": v(2921, 169.07) * mm});
            skLineSegment(sketch, "E12.26.29.0", {"start": v(2933.7, 152.4) * mm, "end": v(2933.7, 156.37) * mm});
            skLineSegment(sketch, "E12.29.29.0", {"start": v(2781.3, 152.4) * mm, "end": v(2781.3, 156.37) * mm});
            skPoint(sketch, "E12.0.30.0", {"position": v(2940.05, 139.7) * mm});
            skPoint(sketch, "E12.1.30.0", {"position": v(3092.45, 139.7) * mm});
            skPoint(sketch, "E12.2.30.0", {"position": v(2940.05, 169.07) * mm});
            skLineSegment(sketch, "E12.3.30.0", {"start": v(2952.75, 169.07) * mm, "end": v(3079.75, 169.07) * mm});
            skLineSegment(sketch, "E12.6.30.0", {"start": v(2952.75, 139.7) * mm, "end": v(3079.75, 139.7) * mm});
            skPoint(sketch, "E12.9.30.0", {"position": v(3092.45, 169.07) * mm});
            skArc(sketch, "E12.10.30.0", {"start": v(2940.05, 152.4) * mm, "mid": v(2943.77, 143.42) * mm, "end": v(2952.75, 139.7) * mm});
            skArc(sketch, "E12.14.30.0", {"start": v(3079.75, 139.7) * mm, "mid": v(3088.73, 143.42) * mm, "end": v(3092.45, 152.4) * mm});
            skArc(sketch, "E12.18.30.0", {"start": v(2952.75, 169.07) * mm, "mid": v(2943.77, 165.35) * mm, "end": v(2940.05, 156.37) * mm});
            skArc(sketch, "E12.22.30.0", {"start": v(3092.45, 156.37) * mm, "mid": v(3088.73, 165.35) * mm, "end": v(3079.75, 169.07) * mm});
            skLineSegment(sketch, "E12.26.30.0", {"start": v(3092.45, 152.4) * mm, "end": v(3092.45, 156.37) * mm});
            skLineSegment(sketch, "E12.29.30.0", {"start": v(2940.05, 152.4) * mm, "end": v(2940.05, 156.37) * mm});
            skPoint(sketch, "E12.0.31.0", {"position": v(3098.8, 139.7) * mm});
            skPoint(sketch, "E12.1.31.0", {"position": v(3251.2, 139.7) * mm});
            skPoint(sketch, "E12.2.31.0", {"position": v(3098.8, 169.07) * mm});
            skLineSegment(sketch, "E12.3.31.0", {"start": v(3111.5, 169.07) * mm, "end": v(3238.5, 169.07) * mm});
            skLineSegment(sketch, "E12.6.31.0", {"start": v(3111.5, 139.7) * mm, "end": v(3238.5, 139.7) * mm});
            skPoint(sketch, "E12.9.31.0", {"position": v(3251.2, 169.07) * mm});
            skArc(sketch, "E12.10.31.0", {"start": v(3098.8, 152.4) * mm, "mid": v(3102.52, 143.42) * mm, "end": v(3111.5, 139.7) * mm});
            skArc(sketch, "E12.14.31.0", {"start": v(3238.5, 139.7) * mm, "mid": v(3247.48, 143.42) * mm, "end": v(3251.2, 152.4) * mm});
            skArc(sketch, "E12.18.31.0", {"start": v(3111.5, 169.07) * mm, "mid": v(3102.52, 165.35) * mm, "end": v(3098.8, 156.37) * mm});
            skArc(sketch, "E12.22.31.0", {"start": v(3251.2, 156.37) * mm, "mid": v(3247.48, 165.35) * mm, "end": v(3238.5, 169.07) * mm});
            skLineSegment(sketch, "E12.26.31.0", {"start": v(3251.2, 152.4) * mm, "end": v(3251.2, 156.37) * mm});
            skLineSegment(sketch, "E12.29.31.0", {"start": v(3098.8, 152.4) * mm, "end": v(3098.8, 156.37) * mm});
            skSolve(sketch);
        }
        {
            var Q0;
            Q0 = qSketchRegion(id + "F2", true);
            extrude(context, id + "F3", {"entities" : qUnion([Q0]), "oppositeDirection" : true, "depth" : 2438.4 * mm, "offsetDistance" : 25.4 * mm});
        }
    });
